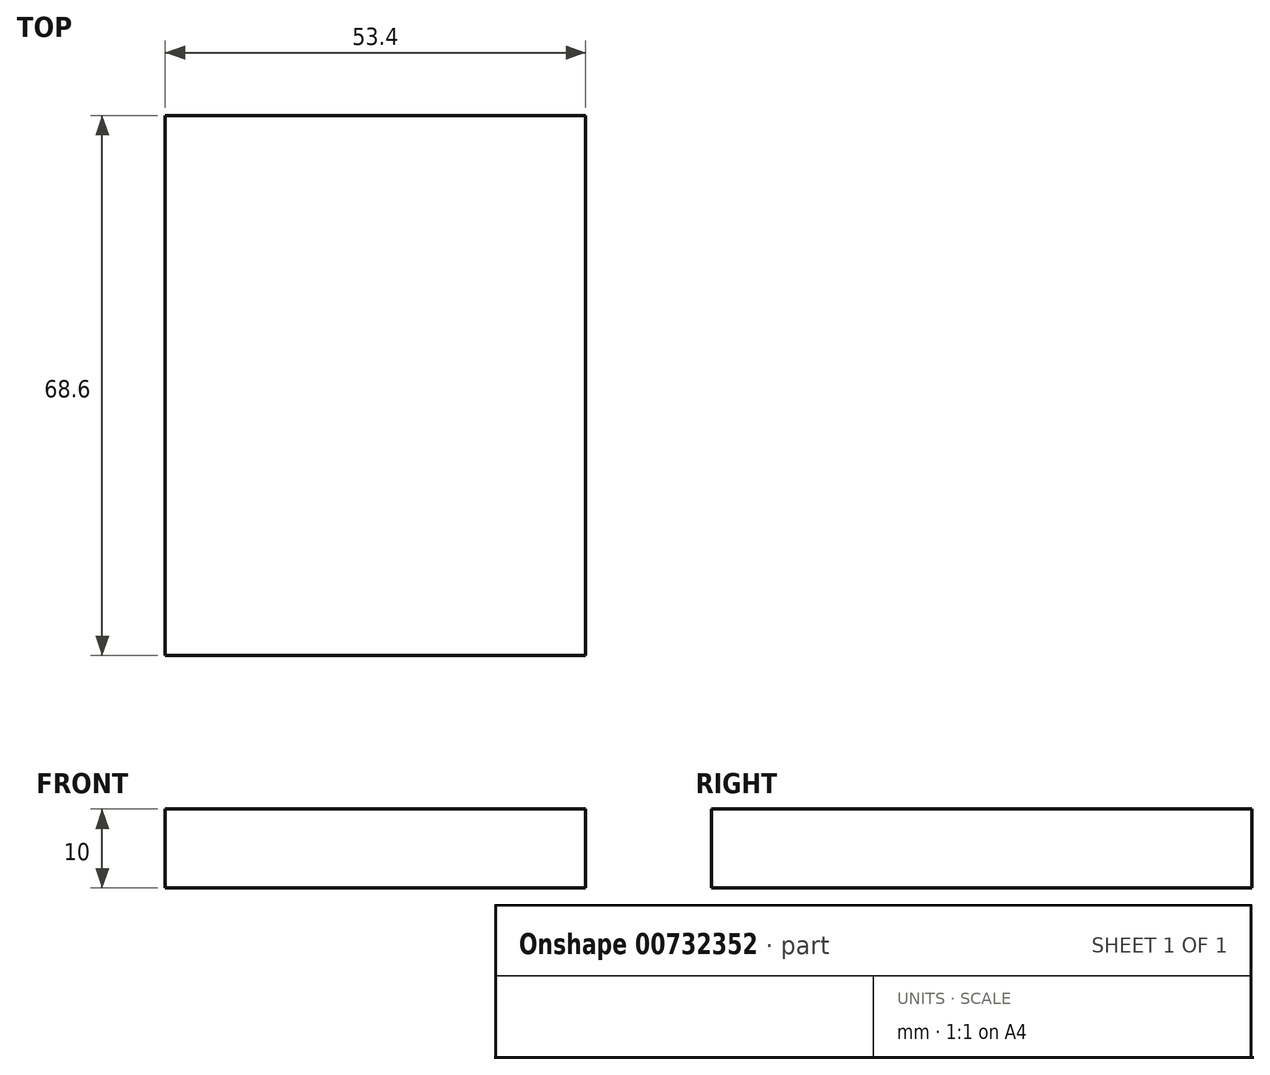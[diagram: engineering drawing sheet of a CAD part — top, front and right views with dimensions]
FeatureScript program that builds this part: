
annotation { "Feature Type Name" : "Feature", "Feature Type Description" : "" }
export const myFeature = defineFeature(function(context is Context, id is Id, definition is map)
    precondition{}
    {
        {
            var Q0;
            Q0=qCreatedBy(makeId("Top.planeOp"),FACE);
            var sketch = newSketch(context, id + "F0", { "sketchPlane" : qUnion([Q0])});
            skLineSegment(sketch, "E0.bottom", {"start": v(-26.7, 0) * mm, "end": v(26.7, 0) * mm});
            skLineSegment(sketch, "E0.top", {"start": v(-26.7, -68.6) * mm, "end": v(26.7, -68.6) * mm});
            skLineSegment(sketch, "E0.left", {"start": v(-26.7, 0) * mm, "end": v(-26.7, -68.6) * mm});
            skLineSegment(sketch, "E0.right", {"start": v(26.7, 0) * mm, "end": v(26.7, -68.6) * mm});
            skSolve(sketch);
        }
        {
            var Q0;
            Q0=makeQuery(id+"F0.imprint","IMPRINT",FACE,{"disambiguationData":[TD([[makeQuery(id+"F0.imprint","IMPRINT",EDGE,{"derivedFrom":sQuery(id+"F0.wireOp",EDGE,"E0.bottom")}),-1.0]])]});
            extrude(context, id + "F1", {"entities" : qUnion([Q0]), "depth" : 10 * mm, "offsetDistance" : 25.4 * mm});
        }
    });
